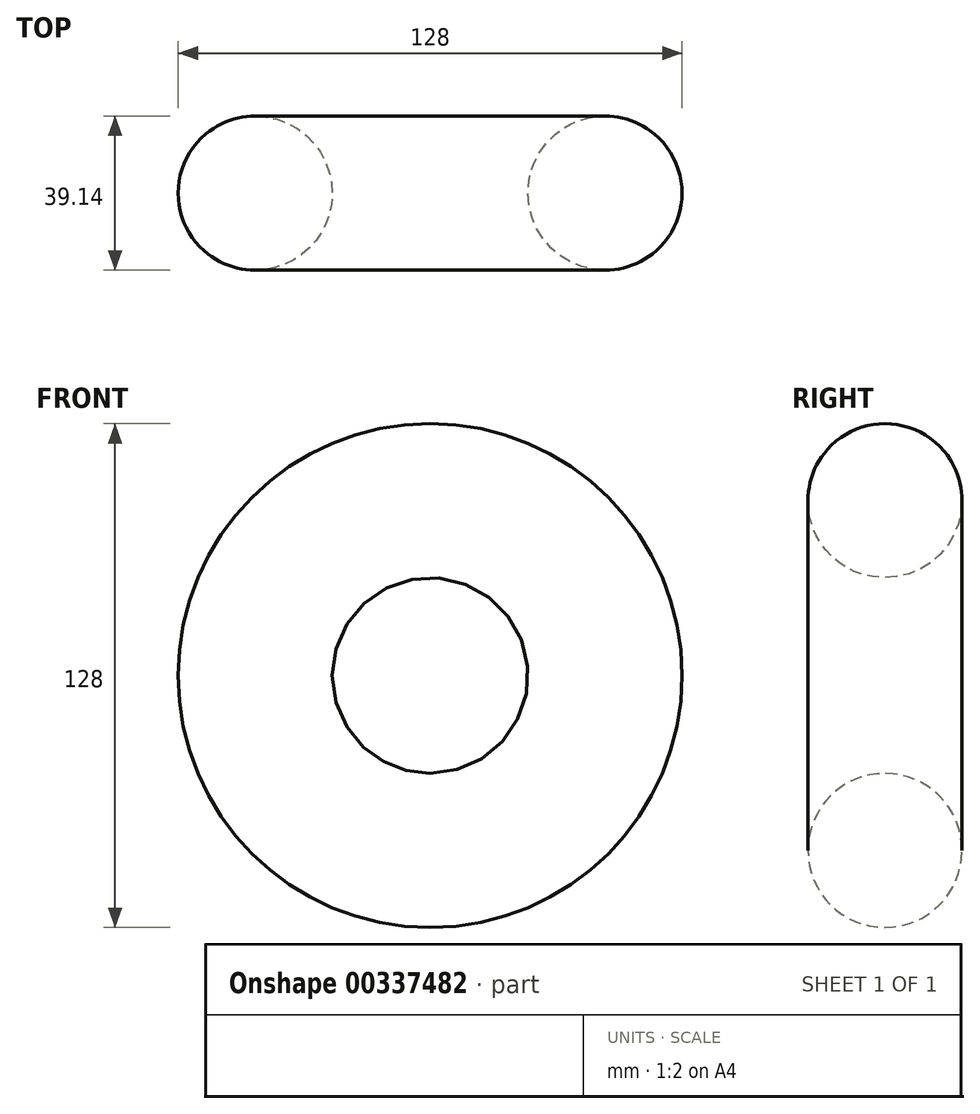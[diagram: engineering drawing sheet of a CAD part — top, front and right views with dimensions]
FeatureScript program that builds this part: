
annotation { "Feature Type Name" : "Feature", "Feature Type Description" : "" }
export const myFeature = defineFeature(function(context is Context, id is Id, definition is map)
    precondition{}
    {
        {
            var Q0;
            Q0=qCreatedBy(makeId("Top.planeOp"),FACE);
            var sketch = newSketch(context, id + "F0", { "sketchPlane" : qUnion([Q0])});
            skCircle(sketch, "E0", {"center": v(-44.43, 10.04) * mm, "radius": 19.57 * mm});
            skSolve(sketch);
        }
        {
            var Q0;
            Q0=qCreatedBy(makeId("Top.planeOp"),FACE);
            var sketch = newSketch(context, id + "F1", { "sketchPlane" : qUnion([Q0])});
            skLineSegment(sketch, "E1", {"start": v(0, 0) * mm, "end": v(0, 20.67) * mm});
            skSolve(sketch);
        }
        {
            var Q0;
            Q0=makeQuery(id+"F0.imprint","IMPRINT",FACE,{"disambiguationData":[TD([[makeQuery(id+"F0.imprint","IMPRINT",EDGE,{"derivedFrom":sQuery(id+"F0.wireOp",EDGE,"E0")}),1.0]])]});
            var Q1;
            Q1=sQuery(id+"F1.wireOp",EDGE,"E1");
            revolve(context, id + "F2", {"entities" : qUnion([Q0]), "axis" : qUnion([Q1]), "revolveType" : RevolveType.FULL});
        }
    });
